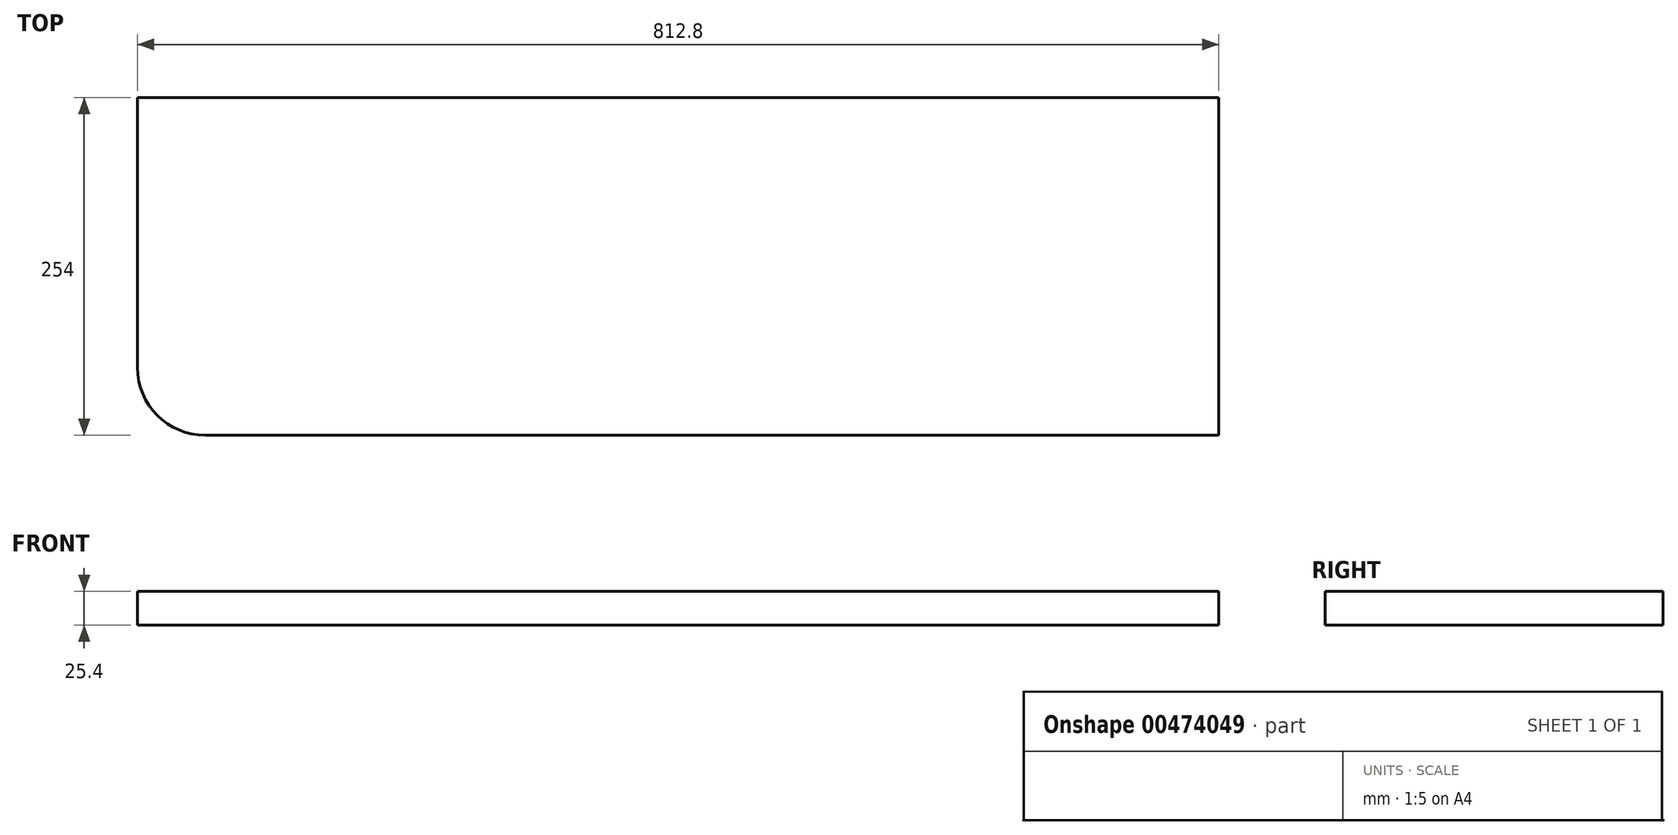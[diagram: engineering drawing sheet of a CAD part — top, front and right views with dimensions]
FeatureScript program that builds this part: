
annotation { "Feature Type Name" : "Feature", "Feature Type Description" : "" }
export const myFeature = defineFeature(function(context is Context, id is Id, definition is map)
    precondition{}
    {
        {
            var Q0;
            Q0=qCreatedBy(makeId("Top.planeOp"),FACE);
            var sketch = newSketch(context, id + "F0", { "sketchPlane" : qUnion([Q0])});
            skLineSegment(sketch, "E0.bottom", {"start": v(-762, -254) * mm, "end": v(0, -254) * mm});
            skLineSegment(sketch, "E0.top", {"start": v(-812.8, 0) * mm, "end": v(0, 0) * mm});
            skLineSegment(sketch, "E0.left", {"start": v(-812.8, -203.2) * mm, "end": v(-812.8, 0) * mm});
            skLineSegment(sketch, "E0.right", {"start": v(0, -254) * mm, "end": v(0, 0) * mm});
            skPoint(sketch, "E1.visualSharp", {"position": v(-812.8, -254) * mm});
            skArc(sketch, "E1.filletArc", {"start": v(-812.8, -203.2) * mm, "mid": v(-797.92, -239.12) * mm, "end": v(-762, -254) * mm});
            skSolve(sketch);
        }
        {
            var Q0;
            Q0=makeQuery(id+"F0.imprint","IMPRINT",FACE,{"disambiguationData":[TD([[makeQuery(id+"F0.imprint","IMPRINT",EDGE,{"derivedFrom":sQuery(id+"F0.wireOp",EDGE,"E0.bottom")}),1.0]])]});
            extrude(context, id + "F1", {"entities" : qUnion([Q0]), "depth" : 25.4 * mm, "offsetDistance" : 25.4 * mm});
        }
    });
